# Revit family: GrabBar-Vitra-ArkitektaSeries-A44375
name_source: partatom
category: Plumbing Fixtures
revit_build: Autodesk Revit 2017 (Build: 20160225_1515(x64)
units: mm (PartAtom-declared; Revit-internal decimal feet)

## family parameters
Cut with Voids When Loaded = No
Host = Face
OmniClass Number = 23.45.00.00
OmniClass Title = Sanitary, Laundry, and Cleaning Equipment
Part Type = Normal
Room Calculation Point = No
Round Connector Dimension = Use Diameter
Shared = Yes

## types (1)
- GrabBar-Vitra-ArkitektaSeries-A44375
    Article No. (default) = A44375
    BIMobject category = Sanitary - Accessories
    Brand = VitrA
    CW Connection = No
    Coating Material = Chrome (Metal)
    Color = Chrome
    Default Elevation = 600 mm
    Description = Arkitekta GrabBar
    Design country = Turkey
    HW Connection = No
    IFC Classification = Railing
    Main Material = Metal
    Manufacturer = Vitra
    Manufacturer name = Vitra
    Masterformat 2014 Code = 01 52 19
    Masterformat 2014 Description = Sanitary Facilities
    Model = A44375
    Mounting type = Wall Mounted
    NBS Referans Code = 64-36
    NBS Referans Description = Handrails
    Nominal Depth (mm) = 80 mm  [stored 0.262467 ft]
    Nominal Height (mm) = 52 mm
    Nominal Width (mm) = 355 mm
    OmniClass Code = 23-17 25 13
    OmniClass Description = Handrails
    Product Properties = Accessible Bathrooms
    Product SKU = A44375
    Product Type = GrabBar
    Product certification = https://www.vitraglobal.com
    Product family = Arkitekta
    Product group = GrabBar
    Product url = https://vitraglobal.com
    Technical description = https://vitraglobal.com
    UNSPSC Code = 301815
    UNSPSC Description = Sanitary ware
    URL = https://vitraglobal.com
    Uniclass 1.4 Code = L4422
    Uniclass 1.4 Description = Hand rails, grab rails
    Uniclass 2.0 Code = PR-64-36
    Uniclass 2.0 Description = Handrails
    Uniclass 2015 Code = Pr_25_30_36
    Uniclass 2015 Name = Handrails
    Uniformat II Code = E20
    Uniformat II Description = FURNISHINGS
    Vent Connection = No
    Warranty Period (Year) = 10
    Waste Connection = No
    Weight Net (kg) = 3
    Youtube = https://www.youtube.com

note: [stored X ft] marks values corroborated as IEEE doubles in the binary element streams (Revit-internal decimal feet)

## geometry (parser evidence)
native form markers: Sweep x3
no freeform markers — native parametric forms only
